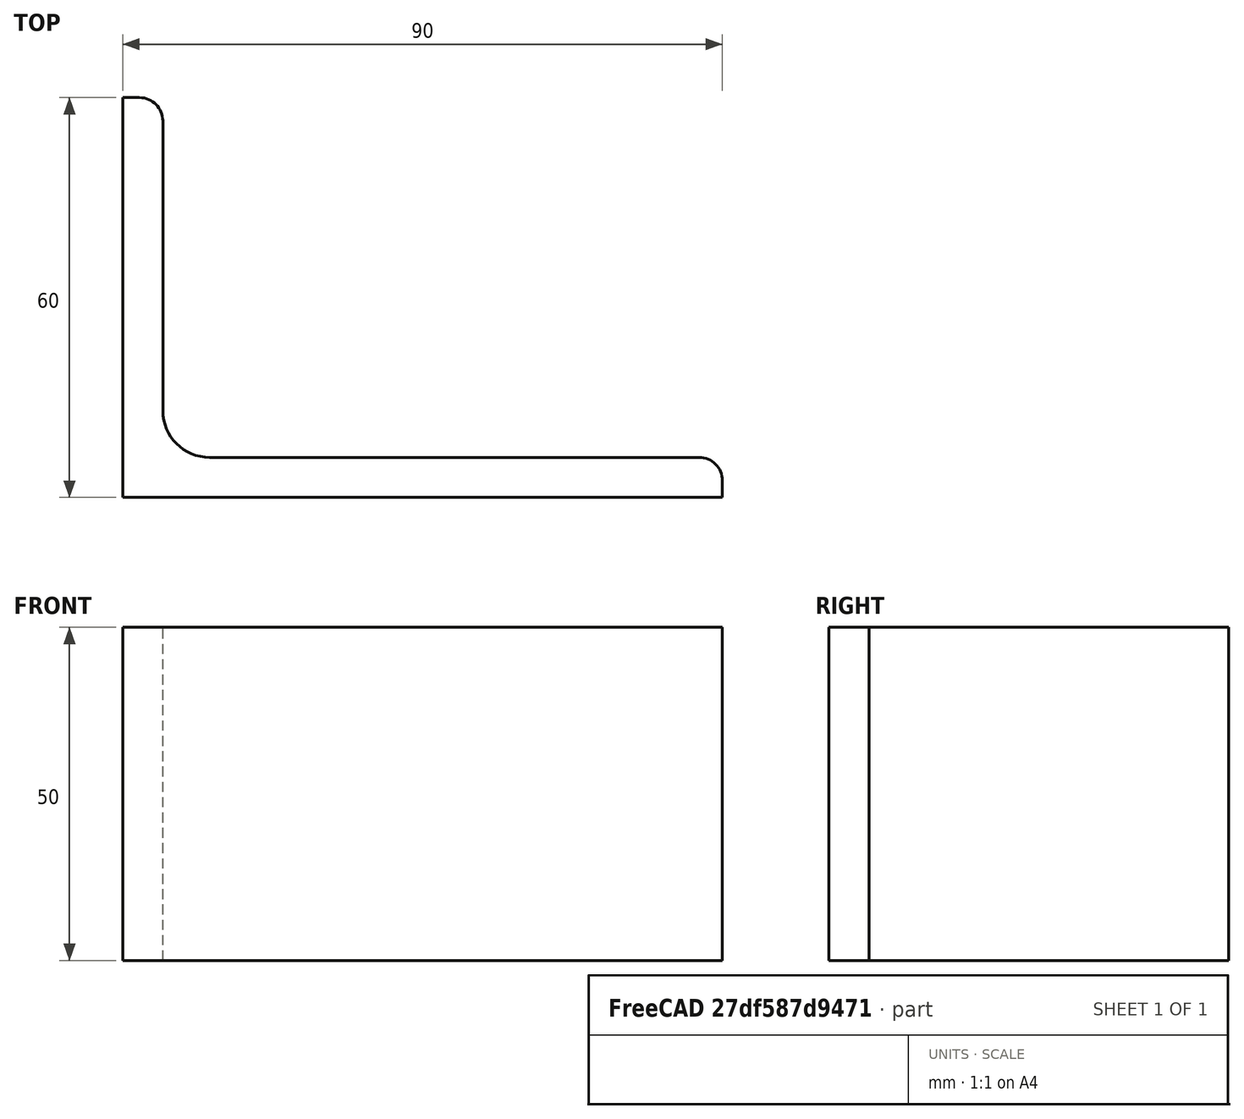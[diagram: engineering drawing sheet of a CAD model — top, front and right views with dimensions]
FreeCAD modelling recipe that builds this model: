
FCSTD DOCUMENT  (FreeCAD 0.15R4671 (Git))
Label: Angle Bar 90x60x6 EN10056 S235JR
License: All rights reserved
LicenseURL: http://en.wikipedia.org/wiki/All_rights_reserved
objects: Sketcher::SketchObject×1, Part::Extrusion×1
note: 2 computed .brp shape members not serialized (recipe doc carries the construction recipe); baked Part::Feature solids carry a one-line shape summary decoded from their .brp

FEATURE [Sketcher::SketchObject] Sketch
  sketch-geometry (9):
    g0: LineSegment StartX=0 StartY=0 StartZ=0 EndX=90 EndY=0 EndZ=0
    g1: LineSegment StartX=90 StartY=0 StartZ=0 EndX=90 EndY=2.5 EndZ=0
    g2: LineSegment StartX=86.5 StartY=6 StartZ=0 EndX=13 EndY=6 EndZ=0
    g3: LineSegment StartX=0 StartY=0 StartZ=0 EndX=0 EndY=60 EndZ=0
    g4: LineSegment StartX=0 StartY=60 StartZ=0 EndX=2.5 EndY=60 EndZ=0
    g5: LineSegment StartX=6 StartY=56.5 StartZ=0 EndX=6 EndY=13 EndZ=0
    g6: ArcOfCircle CenterX=13 CenterY=13 CenterZ=0 NormalX=0 NormalY=0 NormalZ=1 Radius=7 StartAngle=3.14159 EndAngle=4.71239
    g7: ArcOfCircle CenterX=2.5 CenterY=56.5 CenterZ=0 NormalX=0 NormalY=0 NormalZ=1 Radius=3.5 StartAngle=0 EndAngle=1.5708
    g8: ArcOfCircle CenterX=86.5 CenterY=2.5 CenterZ=0 NormalX=0 NormalY=0 NormalZ=1 Radius=3.5 StartAngle=0 EndAngle=1.5708
  constraints (23):
    c: Coincident(g0,g-1)
    c: Horizontal(g0)
    c: Coincident(g1,g0)
    c: Vertical(g1)
    c: Horizontal(g2)
    c: Coincident(g3,g-1)
    c: Vertical(g3)
    c: Coincident(g4,g3)
    c: Horizontal(g4)
    c: Vertical(g5)
    c: Tangent(g5,g6) = -1.5708
    c: Tangent(g2,g6) = 1.5708
    c: Tangent(g4,g7) = 1.5708
    c: Tangent(g5,g7) = 1.5708
    c: Tangent(g2,g8) = -1.5708
    c: Tangent(g1,g8) = -1.5708
    c: DistanceX(g0) = 90
    c: DistanceY(g3) = 60
    c: DistanceY(g0,g2) = 6
    c: DistanceX(g3,g5) = 6
    c: Radius(g6) = 7
    c: Radius(g8) = 3.5
    c: Radius(g7) = 3.5
FEATURE [Part::Extrusion] Extrude  label="Angle Bar 90x60x6 EN10056 S235JR"
  Base = -> Sketch
  Dir = (0,0,50)
  Solid = true
